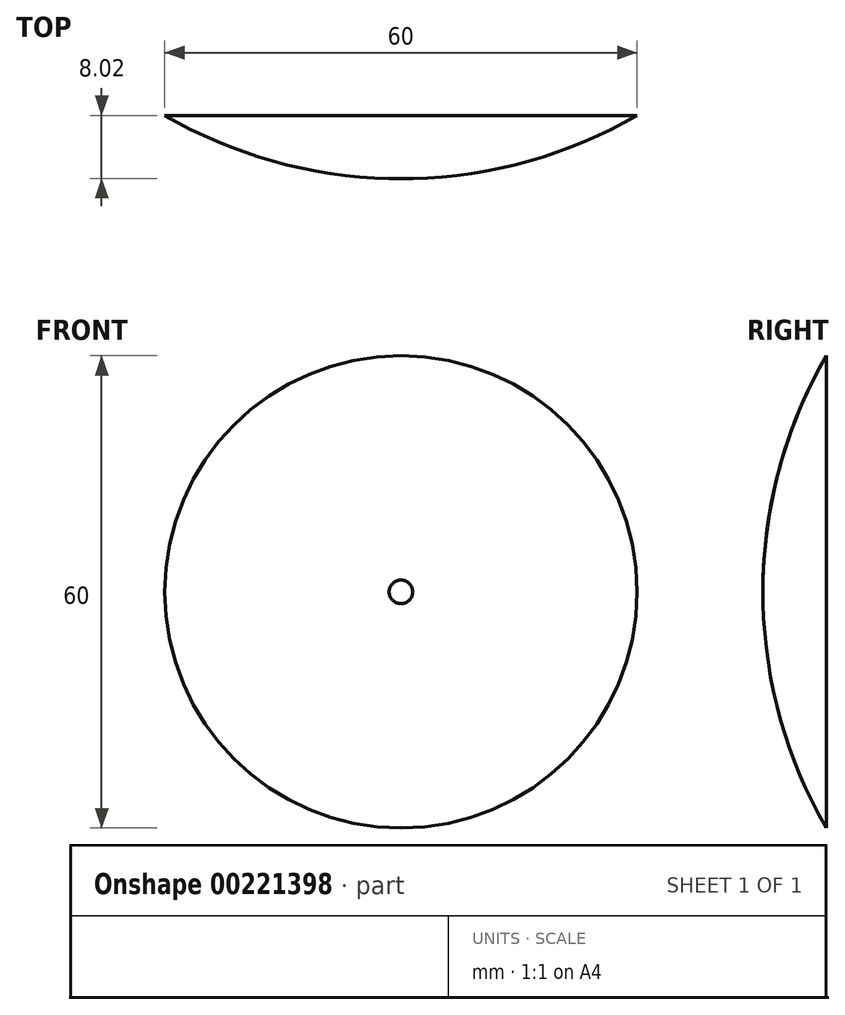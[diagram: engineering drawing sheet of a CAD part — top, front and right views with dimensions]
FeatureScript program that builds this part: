
annotation { "Feature Type Name" : "Feature", "Feature Type Description" : "" }
export const myFeature = defineFeature(function(context is Context, id is Id, definition is map)
    precondition{}
    {
        {
            var Q0;
            Q0=qCreatedBy(makeId("Right.planeOp"),FACE);
            var sketch = newSketch(context, id + "F0", { "sketchPlane" : qUnion([Q0])});
            skArc(sketch, "E0", {"start": v(8.04, 30) * mm, "mid": v(2.24, 16.25) * mm, "end": v(0.02, 1.5) * mm});
            skLineSegment(sketch, "E1", {"start": v(5, 1.5) * mm, "end": v(-5, 1.5) * mm, "construction": true});
            skPoint(sketch, "E2.orphan", {"position": v(0, 0) * mm});
            skSolve(sketch);
        }
        {
            var Q0;
            Q0=qCreatedBy(makeId("Right.planeOp"),FACE);
            var sketch = newSketch(context, id + "F1", { "sketchPlane" : qUnion([Q0])});
            skLineSegment(sketch, "E3", {"start": v(-38.93, 0) * mm, "end": v(43.41, 0) * mm, "construction": true});
            skSolve(sketch);
        }
        {
            var Q0;
            Q0=sQuery(id+"F0.wireOp",EDGE,"E0");
            var Q1;
            Q1=sQuery(id+"F1.wireOp",EDGE,"E3");
            revolve(context, id + "F2", {"bodyType" : ToolBodyType.SURFACE, "surfaceEntities" : qUnion([Q0]), "axis" : qUnion([Q1]), "revolveType" : RevolveType.FULL});
        }
    });
